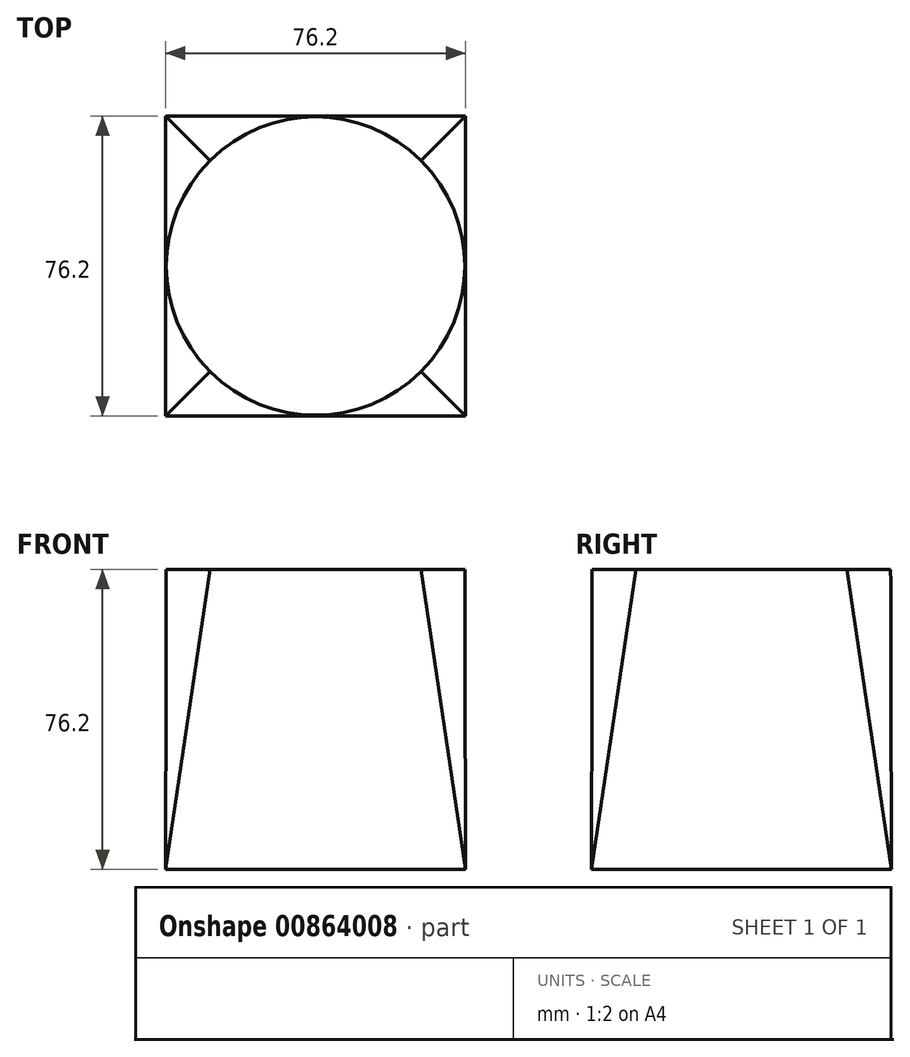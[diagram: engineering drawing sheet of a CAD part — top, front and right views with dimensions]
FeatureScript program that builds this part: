
annotation { "Feature Type Name" : "Feature", "Feature Type Description" : "" }
export const myFeature = defineFeature(function(context is Context, id is Id, definition is map)
    precondition{}
    {
        {
            var Q0;
            Q0=qCreatedBy(makeId("Top.planeOp"),FACE);
            var sketch = newSketch(context, id + "F0", { "sketchPlane" : qUnion([Q0])});
            skLineSegment(sketch, "E0.bottom", {"start": v(-38.1, -38.1) * mm, "end": v(38.1, -38.1) * mm});
            skLineSegment(sketch, "E0.top", {"start": v(-38.1, 38.1) * mm, "end": v(38.1, 38.1) * mm});
            skLineSegment(sketch, "E0.left", {"start": v(-38.1, -38.1) * mm, "end": v(-38.1, 38.1) * mm});
            skLineSegment(sketch, "E0.right", {"start": v(38.1, -38.1) * mm, "end": v(38.1, 38.1) * mm});
            skPoint(sketch, "E0.middle", {"position": v(0, 0) * mm});
            skSolve(sketch);
        }
        {
            var Q0;
            Q0=qCreatedBy(makeId("Top.planeOp"),FACE);
            cPlane(context, id + "F1", {"entities" : qUnion([Q0]), "cplaneType" : CPlaneType.OFFSET, "offset" : 76.2 * mm, "width" : 152.4 * mm, "height" : 152.4 * mm});
        }
        {
            var Q0;
            Q0=qCreatedBy(id+"F1.planeOp",FACE);
            var sketch = newSketch(context, id + "F2", { "sketchPlane" : qUnion([Q0])});
            skCircle(sketch, "E1", {"center": v(0, 0) * mm, "radius": 37.91 * mm});
            skSolve(sketch);
        }
        {
            var Q0;
            Q0=makeQuery(id+"F0.imprint","IMPRINT",FACE,{"disambiguationData":[TD([[makeQuery(id+"F0.imprint","IMPRINT",EDGE,{"derivedFrom":sQuery(id+"F0.wireOp",EDGE,"E0.bottom")}),1.0]])]});
            var Q1;
            Q1=makeQuery(id+"F2.imprint","IMPRINT",FACE,{"disambiguationData":[TD([[makeQuery(id+"F2.imprint","IMPRINT",EDGE,{"derivedFrom":sQuery(id+"F2.wireOp",EDGE,"E1")}),1.0]])]});
            loft(context, id + "F3", {"sheetProfilesArray" : [{ "sheetProfileEntities" : qUnion([Q0]) }, { "sheetProfileEntities" : qUnion([Q1]) }]});
        }
    });
